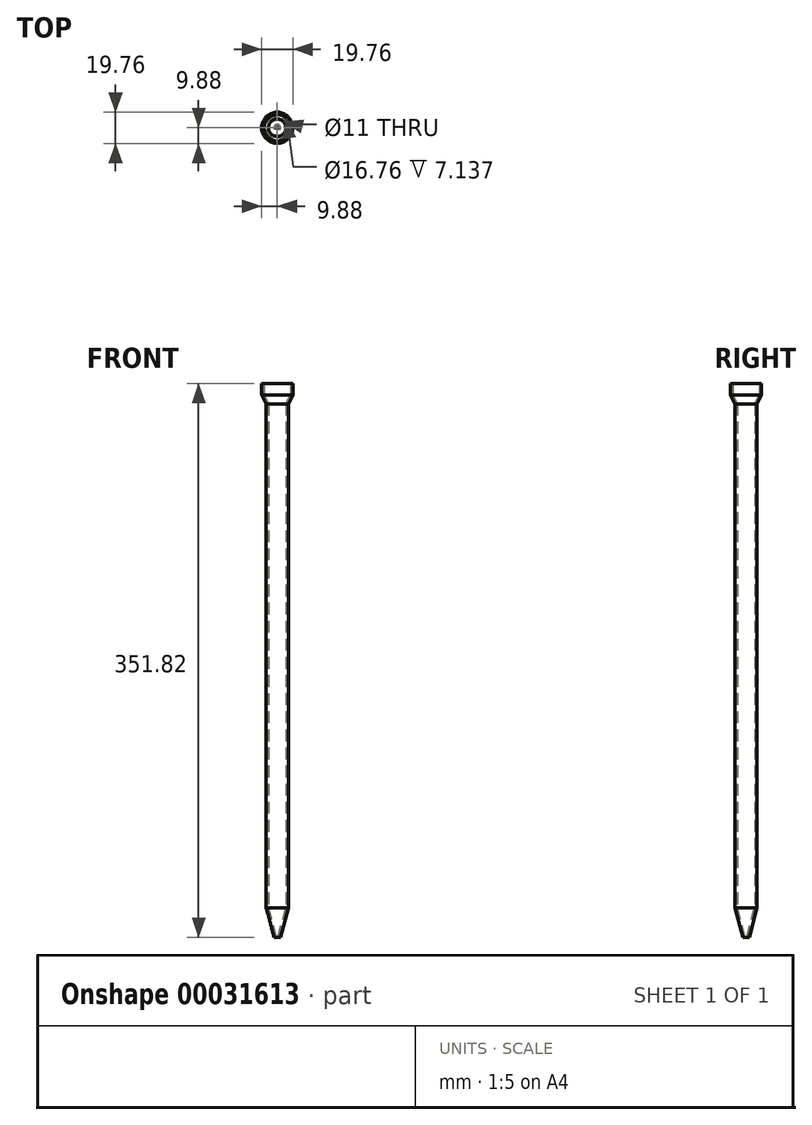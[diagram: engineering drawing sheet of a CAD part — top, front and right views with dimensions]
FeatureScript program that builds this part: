
annotation { "Feature Type Name" : "Feature", "Feature Type Description" : "" }
export const myFeature = defineFeature(function(context is Context, id is Id, definition is map)
    precondition{}
    {
        {
            var Q0;
            Q0=qCreatedBy(makeId("Front.planeOp"),FACE);
            var sketch = newSketch(context, id + "F0", { "sketchPlane" : qUnion([Q0])});
            skLineSegment(sketch, "E0", {"start": v(-9.88, 284.77) * mm, "end": v(-9.88, 277.27) * mm});
            skLineSegment(sketch, "E1", {"start": v(-9.88, 277.27) * mm, "end": v(-7, 271.67) * mm});
            skLineSegment(sketch, "E2", {"start": v(-7, 271.67) * mm, "end": v(-7, -48.33) * mm});
            skLineSegment(sketch, "E3", {"start": v(0, -75.58) * mm, "end": v(0, 303.1) * mm, "construction": true});
            skLineSegment(sketch, "E4", {"start": v(-2.05, -67.05) * mm, "end": v(-7, -48.33) * mm});
            skLineSegment(sketch, "E5.0", {"start": v(-0.6, -66.67) * mm, "end": v(-5.5, -48.14) * mm});
            skLineSegment(sketch, "E5.1", {"start": v(-5.5, 272.03) * mm, "end": v(-5.5, -48.14) * mm});
            skLineSegment(sketch, "E5.2", {"start": v(-8.38, 277.63) * mm, "end": v(-5.5, 272.03) * mm});
            skLineSegment(sketch, "E5.3", {"start": v(-8.38, 284.77) * mm, "end": v(-8.38, 277.63) * mm});
            skLineSegment(sketch, "E6", {"start": v(-2.05, -67.05) * mm, "end": v(-0.6, -66.67) * mm});
            skLineSegment(sketch, "E7", {"start": v(-9.88, 284.77) * mm, "end": v(-8.38, 284.77) * mm});
            skSolve(sketch);
        }
        {
            var Q0;
            Q0=makeQuery(id+"F0.imprint","IMPRINT",FACE,{"disambiguationData":[TD([[makeQuery(id+"F0.imprint","IMPRINT",EDGE,{"derivedFrom":sQuery(id+"F0.wireOp",EDGE,"E0")}),1.0]])]});
            var Q1;
            Q1=sQuery(id+"F0.wireOp",EDGE,"E3");
            revolve(context, id + "F1", {"entities" : qUnion([Q0]), "axis" : qUnion([Q1]), "revolveType" : RevolveType.FULL});
        }
    });
